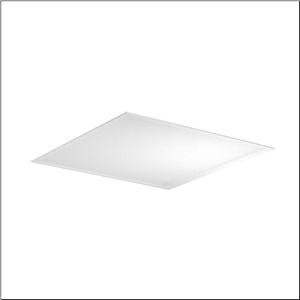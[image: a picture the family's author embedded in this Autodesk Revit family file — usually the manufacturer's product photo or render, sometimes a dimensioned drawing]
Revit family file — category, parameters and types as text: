
# Revit family: apollon_r__21_square_51mq12w72m14_a180
name_source: partatom
category: Lighting Fixtures
units: mm (PartAtom-declared; Revit-internal decimal feet)

## family parameters
Cut with Voids When Loaded = No
Host = Face
Light Source = No
Part Type = Normal
Room Calculation Point = No
Round Connector Dimension = Use Diameter
Shared = No

## types (1)
- --- (1 x LED, 4200 lm, 24.2 W, 4000K)
    Apparent Load = 24 VA
    CIE Flux Codes = 60 87 97 100 100
    Color Rendering = 80
    Color Temperature = 4000K
    Default Elevation = 1800 mm
    Description = Apollon® 21 square, office luminaire, primary optical cover: micro prismatic cover, of PMMA, CAT 2 (L<= 3000cd/m²), light emission: direct distribution, primary light characteristic: symmetric, installation type: lay-in mounting, LED, rated luminous flux: 4.200lm, luminous efficacy: 174lm/W, light colour: 830/840, colour temperature: 3000/4000K, with terminal, 3-pole, mains connection: 220..240V, AC/DC, 0/50..60Hz, rated input power: 24.2W, housing, of aluminium, coated, traffic white (RAL 9016), module: M600, length: 595mm, width: 595mm, height: 30mm, housing upper side, of sheet steel, galvanised, protection rating (complete): IP20, protection rating (lamp compartment, on room side): IP50, insulation class (complete): insulation class II (safety insulation), certification: CE, ENEC, impact resistance: IK03, permissible operating ambient temperature: -20..+45°C, permissible storage temperature: -40..+80°C, packaging unit: 1 piece
    Height = 0 mm  [stored 0 ft]
    Lamp = 1 x LED
    Lamp Light Flux = 4200 lm
    Lamp Power = 24.2 W
    Lamp count = 1
    Length = 595 mm
    Luminous efficacy = 174 lm/W
    Manufacturer = Siteco
    ModVariant = No
    Model = 51MQ12W72M14
    Mounting Place = Ceiling
    Mounting Type = Recessed
    Number of Poles = 1
    OnlyDefault = Yes
    Power Factor = 1
    Product Name = Apollon® 21 square
    Product group = office luminaire | ceiling recessed
    ProductGroupID = 401
    Protection Class = Protection class II
    Protection Degree = IP 20
    RLX_Detail_Level = 1
    RLX_Emergency_Light_Flux = 0 lm
    RLX_Emergency_Type = 0
    RLX_Emergency_Type_DB = No
    RlxData = <blob elided: 12709 chars, md5=6f0dd209>
    Socket = socket
    Standby Power = 0 W
    System Light Flux = 4200 lm
    System Power = 24 W
    Type Comments = factory setting
    Type Image = l_1291049.jpg
    URL = http://relux.com
    VarID = @adj_026993
    Voltage = 0 V
    Weight = 0.00 kg
    Width = 595 mm

note: [stored X ft] marks values corroborated as IEEE doubles in the binary element streams (Revit-internal decimal feet)

## geometry (parser evidence)
native form markers: Sweep x9
no freeform markers — native parametric forms only
